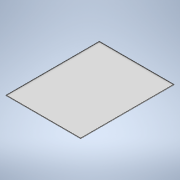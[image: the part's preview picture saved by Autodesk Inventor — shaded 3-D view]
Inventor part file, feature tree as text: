
AUTODESK INVENTOR PART (.ipt)
format: ipt  version: 2021 (Build 250183000, 183)  size: 104,960 bytes
history: native  units: mm
features: extrude x2, sketch x2
ambient origin geometry x8: Origin, YZ Plane, XZ Plane, XY Plane, X Axis, Y Axis, Z Axis, Center Point
bodies: Solid1 (feature_tree)
feature tree (4):
  extrude  "Extrusion1"  Depth=1600.0mm
  extrude  "Extrusion2"  Depth=5.0mm
  sketch  "Sketch1"  dims[d0=2000.0mm d1=1600.0mm]
  sketch  "Sketch2"  dims[d2=12.0mm d3=0.0mm d4=5.0mm d5=10.0mm d6=0.0mm]
